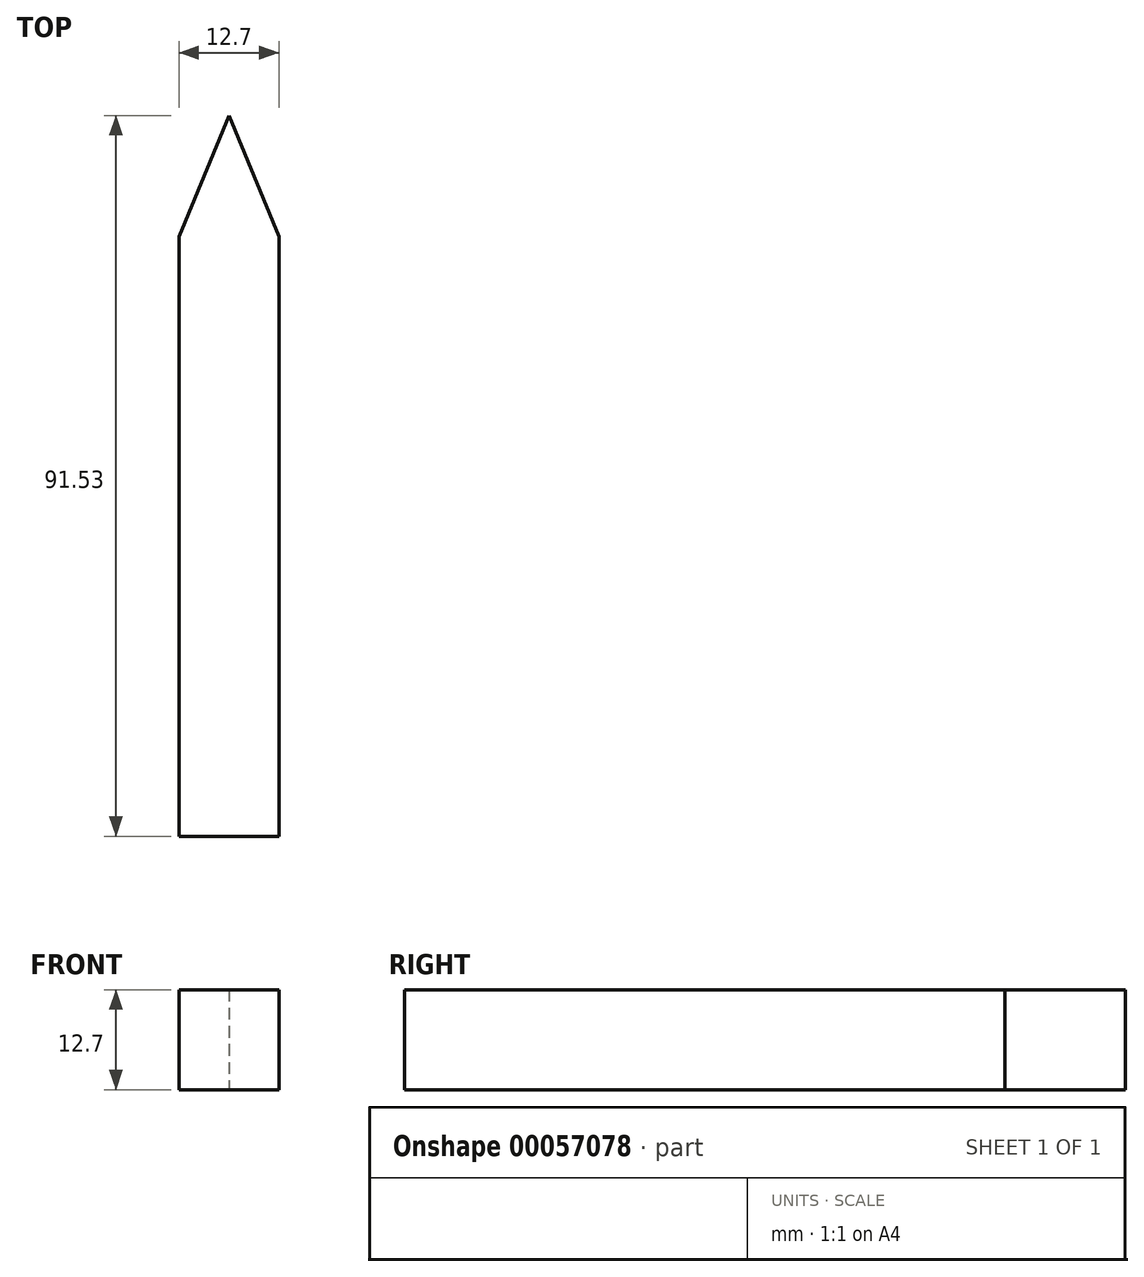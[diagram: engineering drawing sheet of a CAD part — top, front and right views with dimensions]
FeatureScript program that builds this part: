
annotation { "Feature Type Name" : "Feature", "Feature Type Description" : "" }
export const myFeature = defineFeature(function(context is Context, id is Id, definition is map)
    precondition{}
    {
        {
            var Q0;
            Q0=qCreatedBy(makeId("Top.planeOp"),FACE);
            var sketch = newSketch(context, id + "F0", { "sketchPlane" : qUnion([Q0])});
            skLineSegment(sketch, "E0", {"start": v(-6.35, 25.4) * mm, "end": v(-6.35, -50.8) * mm});
            skLineSegment(sketch, "E1", {"start": v(-6.35, -50.8) * mm, "end": v(6.35, -50.8) * mm});
            skLineSegment(sketch, "E2", {"start": v(6.35, -50.8) * mm, "end": v(6.35, 25.4) * mm});
            skLineSegment(sketch, "E3", {"start": v(-6.35, 25.4) * mm, "end": v(0, 40.73) * mm});
            skLineSegment(sketch, "E4", {"start": v(0, 40.73) * mm, "end": v(6.35, 25.4) * mm});
            skSolve(sketch);
        }
        {
            var Q0;
            Q0=makeQuery(id+"F0.imprint","IMPRINT",FACE,{"disambiguationData":[TD([[makeQuery(id+"F0.imprint","IMPRINT",EDGE,{"derivedFrom":sQuery(id+"F0.wireOp",EDGE,"E0")}),1.0]])]});
            extrude(context, id + "F1", {"entities" : qUnion([Q0]), "depth" : 12.7 * mm});
        }
    });
